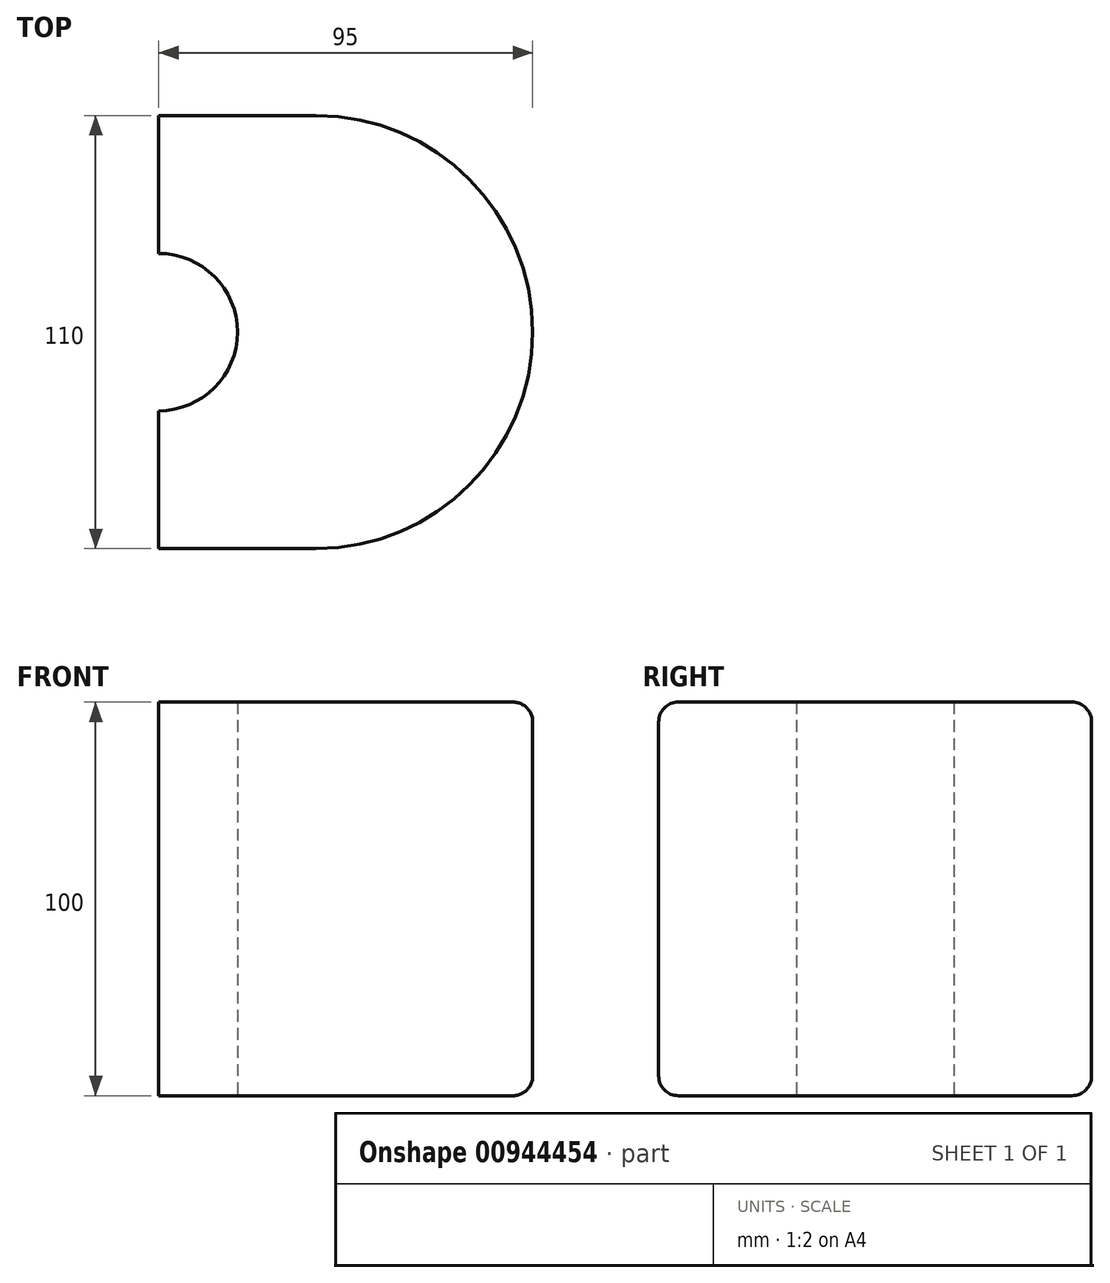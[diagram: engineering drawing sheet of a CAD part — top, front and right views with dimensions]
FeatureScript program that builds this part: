
annotation { "Feature Type Name" : "Feature", "Feature Type Description" : "" }
export const myFeature = defineFeature(function(context is Context, id is Id, definition is map)
    precondition{}
    {
        {
            var Q0;
            Q0=qCreatedBy(makeId("Top.planeOp"),FACE);
            var sketch = newSketch(context, id + "F0", { "sketchPlane" : qUnion([Q0])});
            skArc(sketch, "E0", {"start": v(0, -20) * mm, "mid": v(20, 0) * mm, "end": v(0, 20) * mm});
            skLineSegment(sketch, "E1", {"start": v(0, 20) * mm, "end": v(0, 55) * mm});
            skLineSegment(sketch, "E2", {"start": v(0, -20) * mm, "end": v(0, -55) * mm});
            skLineSegment(sketch, "E3", {"start": v(0, 55) * mm, "end": v(40, 55) * mm});
            skLineSegment(sketch, "E4", {"start": v(0, -55) * mm, "end": v(40, -55) * mm});
            skArc(sketch, "E5", {"start": v(40, -55) * mm, "mid": v(95, 0) * mm, "end": v(40, 55) * mm});
            skSolve(sketch);
        }
        {
            var Q0;
            Q0=makeQuery(id+"F0.imprint","IMPRINT",FACE,{"disambiguationData":[TD([[makeQuery(id+"F0.imprint","IMPRINT",EDGE,{"derivedFrom":sQuery(id+"F0.wireOp",EDGE,"E0")}),-1.0]])]});
            extrude(context, id + "F1", {"entities" : qUnion([Q0]), "depth" : 100 * mm, "offsetDistance" : 25 * mm});
        }
        {
            var Q0;
            Q0=makeQuery(id+"F1.opExtrude","CAP_EDGE",EDGE,{"disambiguationData":[OSD([sQuery(id+"F0.wireOp",EDGE,"E5")])],"isStart":false});
            var Q1;
            Q1=makeQuery(id+"F1.opExtrude","CAP_EDGE",EDGE,{"disambiguationData":[OSD([sQuery(id+"F0.wireOp",EDGE,"E5")])],"isStart":true});
            fillet(context, id + "F2", {"entities" : qUnion([Q0, Q1]), "radius" : 5 * mm, "tangentPropagation" : true, "allowEdgeOverflow" : false});
        }
    });
